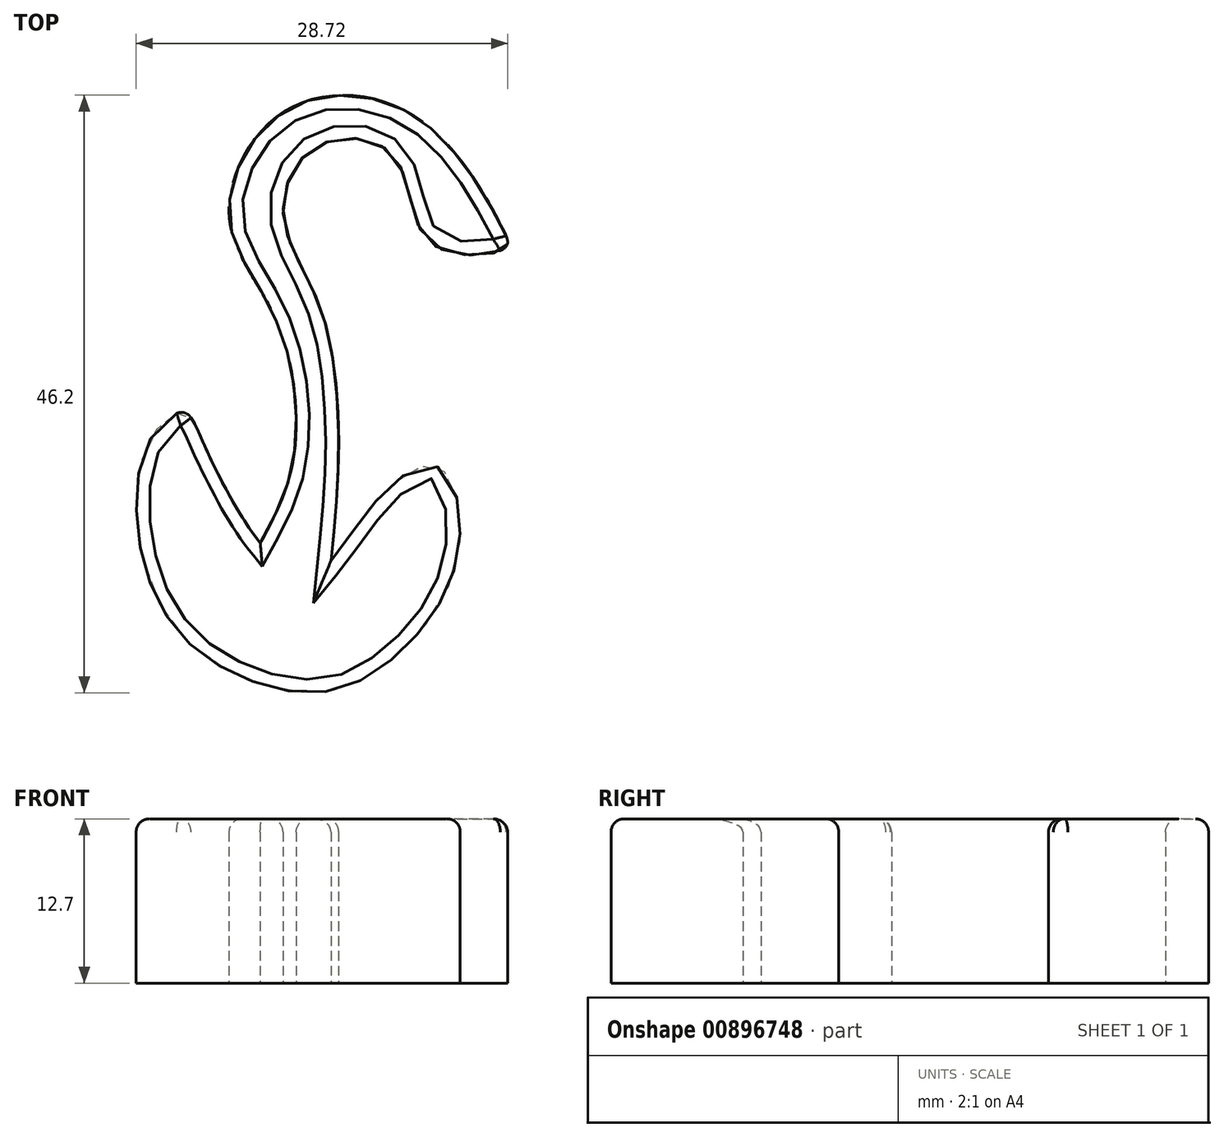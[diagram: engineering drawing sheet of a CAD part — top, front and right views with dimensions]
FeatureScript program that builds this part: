
annotation { "Feature Type Name" : "Feature", "Feature Type Description" : "" }
export const myFeature = defineFeature(function(context is Context, id is Id, definition is map)
    precondition{}
    {
        {
            var Q0;
            Q0=qCreatedBy(makeId("Top.planeOp"),FACE);
            var sketch = newSketch(context, id + "F0", { "sketchPlane" : qUnion([Q0])});
            skFitSpline(sketch, "E0", {"points": [v(-13, 6.65) * mm, v(-8.37, -1.57) * mm, v(-4.78, -4.13) * mm, v(-2.9, -2.94) * mm, v(1.38, 2.54) * mm, v(5.49, 4.25) * mm, v(6.69, -3.45) * mm, v(0, -11.84) * mm, v(-5.98, -13.03) * mm, v(-15.39, -7.56) * mm, v(-17.27, 5.62) * mm, v(-14.36, 8.53) * mm, v(-13, 6.65) * mm]});
            skFitSpline(sketch, "E1", {"points": [v(-8.37, -1.57) * mm, v(-5.8, 4.94) * mm, v(-7.18, 15.72) * mm, v(-10.77, 23.59) * mm, v(-6.5, 31.8) * mm, v(3.78, 31.29) * mm, v(10.28, 22.9) * mm, v(10.5, 21.22) * mm, v(4.8, 21.63) * mm, v(1.96, 28.34) * mm, v(-4.04, 29.06) * mm, v(-6.59, 23.66) * mm, v(-3.74, 16.64) * mm, v(-2.31, 5.25) * mm, v(-2.9, -2.94) * mm], "startDerivative": vector(46.93, 85.62) * mm, "endDerivative": vector(-10.88, -103.24) * mm});
            skSolve(sketch);
        }
        {
            var Q0;
            Q0 = qSketchRegion(id + "F0", true);
            extrude(context, id + "F1", {"entities" : qUnion([Q0]), "depth" : 12.7 * mm, "offsetDistance" : 25.4 * mm});
        }
        {
            var Q0;
            Q0=makeQuery(id+"F1.opExtrude","CAP_EDGE",EDGE,{"disambiguationData":[OSD([sQuery(id+"F0.wireOp",EDGE,"E0")])],"isStart":false});
            var Q1;
            Q1=makeQuery(id+"F1.opExtrude","CAP_EDGE",EDGE,{"disambiguationData":[OSD([sQuery(id+"F0.wireOp",EDGE,"E1")])],"isStart":false});
            fillet(context, id + "F2", {"entities" : qUnion([Q0, Q1]), "radius" : 1.02 * mm, "tangentPropagation" : true, "allowEdgeOverflow" : false});
        }
    });
